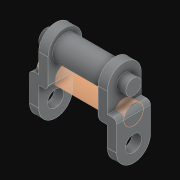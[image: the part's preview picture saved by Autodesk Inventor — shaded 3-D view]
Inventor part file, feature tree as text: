
AUTODESK INVENTOR PART (.ipt)
format: ipt  version: 2021 (Build 250183000, 183)  size: 162,304 bytes
history: native  units: in
note: dims shown in document units (in); Inventor stores cm internally (conversion verified against a paired STEP export)
features: sketch x1, other x1, extrude x1
ambient origin geometry x8: Origin, YZ Plane, XZ Plane, XY Plane, X Axis, Y Axis, Z Axis, Center Point
bodies: Solid2 (feature_tree), Solid1 (feature_tree)
feature tree (3):
  sketch  "Sketch1"  dims[d0=0.1in d1=1.0in d2=0.0in]
  other  "Srf1"
  extrude  "ExtrusionSrf1"  Depth=1.0in TaperAngle=0.0deg
